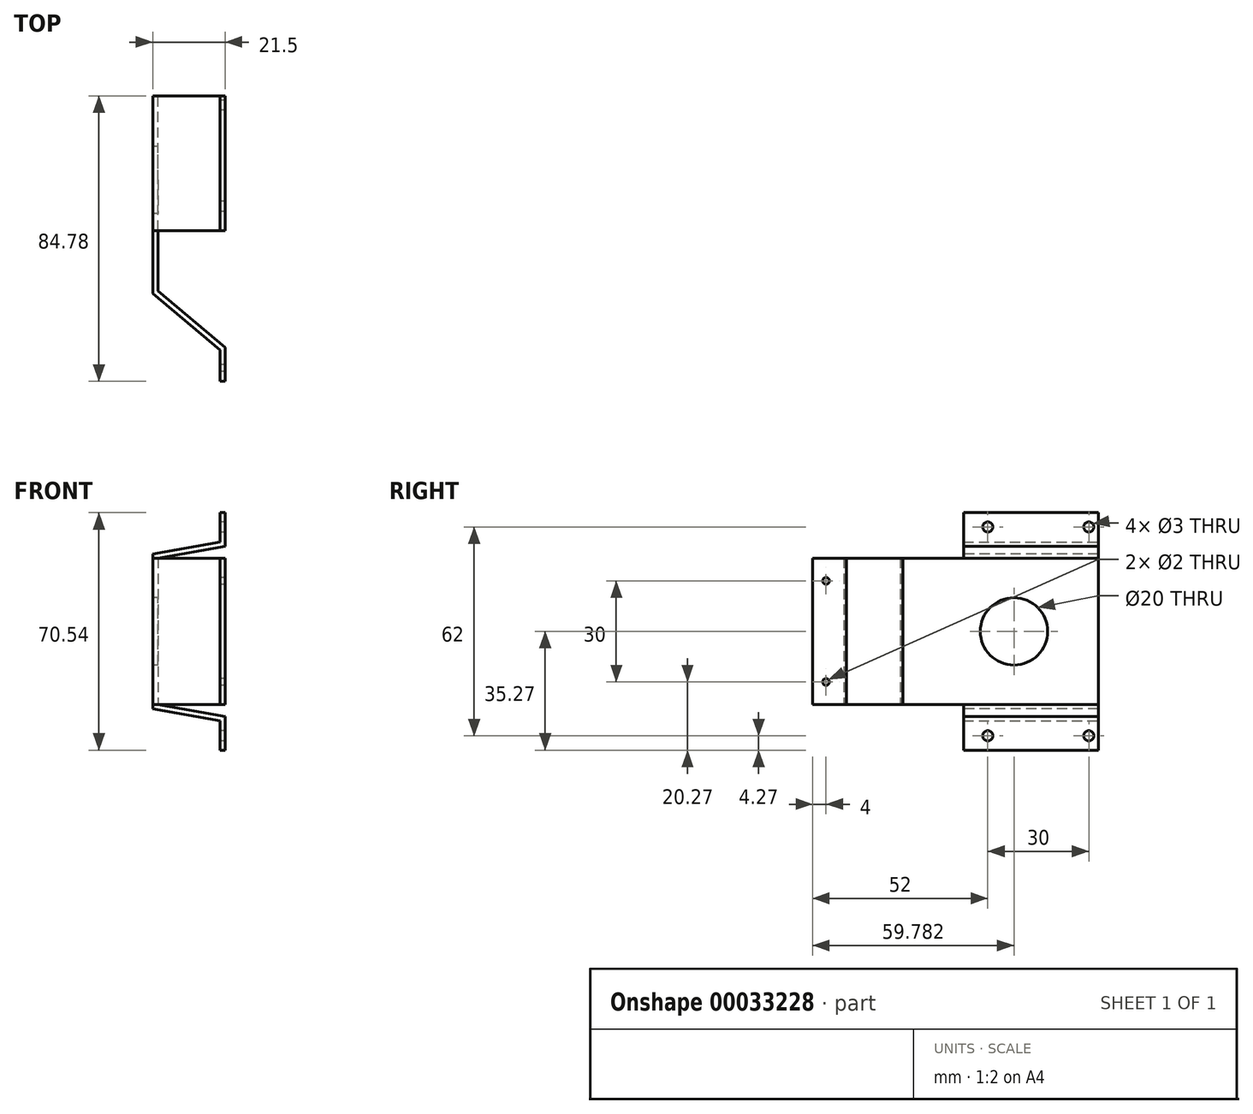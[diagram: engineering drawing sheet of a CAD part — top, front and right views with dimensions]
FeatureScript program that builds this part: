
annotation { "Feature Type Name" : "Feature", "Feature Type Description" : "" }
export const myFeature = defineFeature(function(context is Context, id is Id, definition is map)
    precondition{}
    {
        {
            var Q0;
            Q0=qCreatedBy(makeId("Top.planeOp"),FACE);
            var sketch = newSketch(context, id + "F0", { "sketchPlane" : qUnion([Q0])});
            skLineSegment(sketch, "E0", {"start": v(-21.5, 74.78) * mm, "end": v(-21.5, 16.08) * mm});
            skLineSegment(sketch, "E1", {"start": v(-21.5, 16.08) * mm, "end": v(-1.5, -0.7) * mm});
            skLineSegment(sketch, "E2", {"start": v(-1.5, -0.7) * mm, "end": v(-1.5, -10) * mm});
            skLineSegment(sketch, "E3", {"start": v(-21.5, 74.78) * mm, "end": v(-20, 74.78) * mm});
            skLineSegment(sketch, "E4", {"start": v(-20, 74.78) * mm, "end": v(-20, 16.78) * mm});
            skLineSegment(sketch, "E5", {"start": v(-20, 16.78) * mm, "end": v(0, 0) * mm});
            skLineSegment(sketch, "E6", {"start": v(0, 0) * mm, "end": v(0, -10) * mm});
            skLineSegment(sketch, "E7", {"start": v(-1.5, -10) * mm, "end": v(0, -10) * mm});
            skSolve(sketch);
        }
        {
            var Q0;
            Q0 = qSketchRegion(id + "F0", true);
            extrude(context, id + "F1", {"entities" : qUnion([Q0]), "depth" : (43 + 3) * mm});
        }
        {
            var Q0;
            Q0=makeQuery(id+"F1.opExtrude","SWEPT_FACE",FACE,{"disambiguationData":[OSD([sQuery(id+"F0.wireOp",EDGE,"E2")])]});
            var sketch = newSketch(context, id + "F2", { "sketchPlane" : qUnion([Q0])});
            skLineSegment(sketch, "E8", {"start": v(10, 23) * mm, "end": v(0.7, 23) * mm, "construction": true});
            skCircle(sketch, "E9", {"center": v(6, 8) * mm, "radius": 1 * mm});
            skCircle(sketch, "E10.MirrorC", {"center": v(6, 38) * mm, "radius": 1 * mm});
            skSolve(sketch);
        }
        {
            var Q0;
            Q0 = qSketchRegion(id + "F2", true);
            extrude(context, id + "F3", {"entities" : qUnion([Q0]), "operationType" : NewBodyOperationType.REMOVE, "endBound" : BoundingType.UP_TO_NEXT, "oppositeDirection" : true, "depth" : 25 * mm});
        }
        {
            var Q0;
            Q0=makeQuery(id+"F1.opExtrude","SWEPT_FACE",FACE,{"disambiguationData":[OSD([sQuery(id+"F0.wireOp",EDGE,"E3")])]});
            var sketch = newSketch(context, id + "F4", { "sketchPlane" : qUnion([Q0])});
            skLineSegment(sketch, "E11", {"start": v(0, 48.27) * mm, "end": v(20, 44.74) * mm});
            skLineSegment(sketch, "E12", {"start": v(0, 48.27) * mm, "end": v(0, 58.27) * mm});
            skLineSegment(sketch, "E13", {"start": v(0, 58.27) * mm, "end": v(1.5, 58.27) * mm});
            skLineSegment(sketch, "E14", {"start": v(1.5, 49.53) * mm, "end": v(21.5, 46) * mm});
            skLineSegment(sketch, "E15", {"start": v(1.5, 58.27) * mm, "end": v(1.5, 49.53) * mm});
            skLineSegment(sketch, "E16", {"start": v(20, 44.74) * mm, "end": v(21.5, 44.74) * mm});
            skLineSegment(sketch, "E17", {"start": v(21.5, 44.74) * mm, "end": v(21.5, 46) * mm});
            skLineSegment(sketch, "E18", {"start": v(21.5, 23) * mm, "end": v(0, 23) * mm, "construction": true});
            skLineSegment(sketch, "E19.MirrorCS", {"start": v(20, 1.26) * mm, "end": v(21.5, 1.26) * mm});
            skLineSegment(sketch, "E20.MirrorCS", {"start": v(0, -12.27) * mm, "end": v(1.5, -12.27) * mm});
            skLineSegment(sketch, "E21.MirrorCS", {"start": v(21.5, 1.26) * mm, "end": v(21.5, 0) * mm});
            skLineSegment(sketch, "E22.MirrorCS", {"start": v(0, -2.27) * mm, "end": v(0, -12.27) * mm});
            skLineSegment(sketch, "E23.MirrorCS", {"start": v(0, -2.27) * mm, "end": v(20, 1.26) * mm});
            skLineSegment(sketch, "E24.MirrorCS", {"start": v(1.5, -12.27) * mm, "end": v(1.5, -3.53) * mm});
            skLineSegment(sketch, "E25.MirrorCS", {"start": v(1.5, -3.53) * mm, "end": v(21.5, 0) * mm});
            skSolve(sketch);
        }
        {
            var Q0;
            Q0 = qSketchRegion(id + "F4", true);
            extrude(context, id + "F5", {"entities" : qUnion([Q0]), "operationType" : NewBodyOperationType.ADD, "oppositeDirection" : true, "depth" : 40 * mm});
        }
        {
            var Q0;
            Q0=makeQuery(id+"F5.opExtrude","SWEPT_FACE",FACE,{"disambiguationData":[OSD([sQuery(id+"F4.wireOp",EDGE,"E24.MirrorCS")])]});
            var sketch = newSketch(context, id + "F6", { "sketchPlane" : qUnion([Q0])});
            skCircle(sketch, "E26", {"center": v(-72, -8) * mm, "radius": 1.5 * mm});
            skLineSegment(sketch, "E27.0", {"start": v(-74.78, 46) * mm, "end": v(-74.78, 0) * mm, "construction": true});
            skLineSegment(sketch, "E28", {"start": v(-74.78, 23) * mm, "end": v(0, 23) * mm, "construction": true});
            skCircle(sketch, "E29", {"center": v(-42, -8) * mm, "radius": 1.5 * mm});
            skCircle(sketch, "E30.MirrorC", {"center": v(-42, 54) * mm, "radius": 1.5 * mm});
            skCircle(sketch, "E31.MirrorC", {"center": v(-72, 54) * mm, "radius": 1.5 * mm});
            skSolve(sketch);
        }
        {
            var Q0;
            Q0 = qSketchRegion(id + "F6", true);
            extrude(context, id + "F7", {"entities" : qUnion([Q0]), "operationType" : NewBodyOperationType.REMOVE, "endBound" : BoundingType.UP_TO_NEXT, "oppositeDirection" : true, "depth" : 25 * mm});
        }
        {
            var Q0;
            Q0=makeQuery(id+"F1.opExtrude","SWEPT_FACE",FACE,{"disambiguationData":[OSD([sQuery(id+"F0.wireOp",EDGE,"E0")])]});
            var sketch = newSketch(context, id + "F8", { "sketchPlane" : qUnion([Q0])});
            skCircle(sketch, "E32", {"center": v(-49.78, 23) * mm, "radius": 10 * mm});
            skPoint(sketch, "E32.centerSnap0", {"position": v(-74.78, 23) * mm});
            skSolve(sketch);
        }
        {
            var Q0;
            Q0 = qSketchRegion(id + "F8", true);
            extrude(context, id + "F9", {"entities" : qUnion([Q0]), "operationType" : NewBodyOperationType.REMOVE, "endBound" : BoundingType.UP_TO_NEXT, "oppositeDirection" : true, "depth" : 25 * mm});
        }
        {
            var Q0;
            Q0=makeQuery(id+"F1.opExtrude","CAP_FACE",FACE,{"disambiguationData":[OSD([sQuery(id+"F0.wireOp",EDGE,"E0"),sQuery(id+"F0.wireOp",EDGE,"E1"),sQuery(id+"F0.wireOp",EDGE,"E2"),sQuery(id+"F0.wireOp",EDGE,"E3"),sQuery(id+"F0.wireOp",EDGE,"E4"),sQuery(id+"F0.wireOp",EDGE,"E5"),sQuery(id+"F0.wireOp",EDGE,"E6"),sQuery(id+"F0.wireOp",EDGE,"E7")])],"isStart":true});
            extrude(context, id + "F10", {"entities" : qUnion([Q0]), "operationType" : NewBodyOperationType.REMOVE, "oppositeDirection" : true, "depth" : (1.5 - 0.24) * mm});
        }
        {
            var Q0;
            Q0=makeQuery(id+"F1.opExtrude","CAP_FACE",FACE,{"disambiguationData":[OSD([sQuery(id+"F0.wireOp",EDGE,"E0"),sQuery(id+"F0.wireOp",EDGE,"E1"),sQuery(id+"F0.wireOp",EDGE,"E2"),sQuery(id+"F0.wireOp",EDGE,"E3"),sQuery(id+"F0.wireOp",EDGE,"E4"),sQuery(id+"F0.wireOp",EDGE,"E5"),sQuery(id+"F0.wireOp",EDGE,"E6"),sQuery(id+"F0.wireOp",EDGE,"E7")])],"isStart":false});
            extrude(context, id + "F11", {"entities" : qUnion([Q0]), "operationType" : NewBodyOperationType.REMOVE, "oppositeDirection" : true, "depth" : (1.5 - 0.24) * mm});
        }
    });
